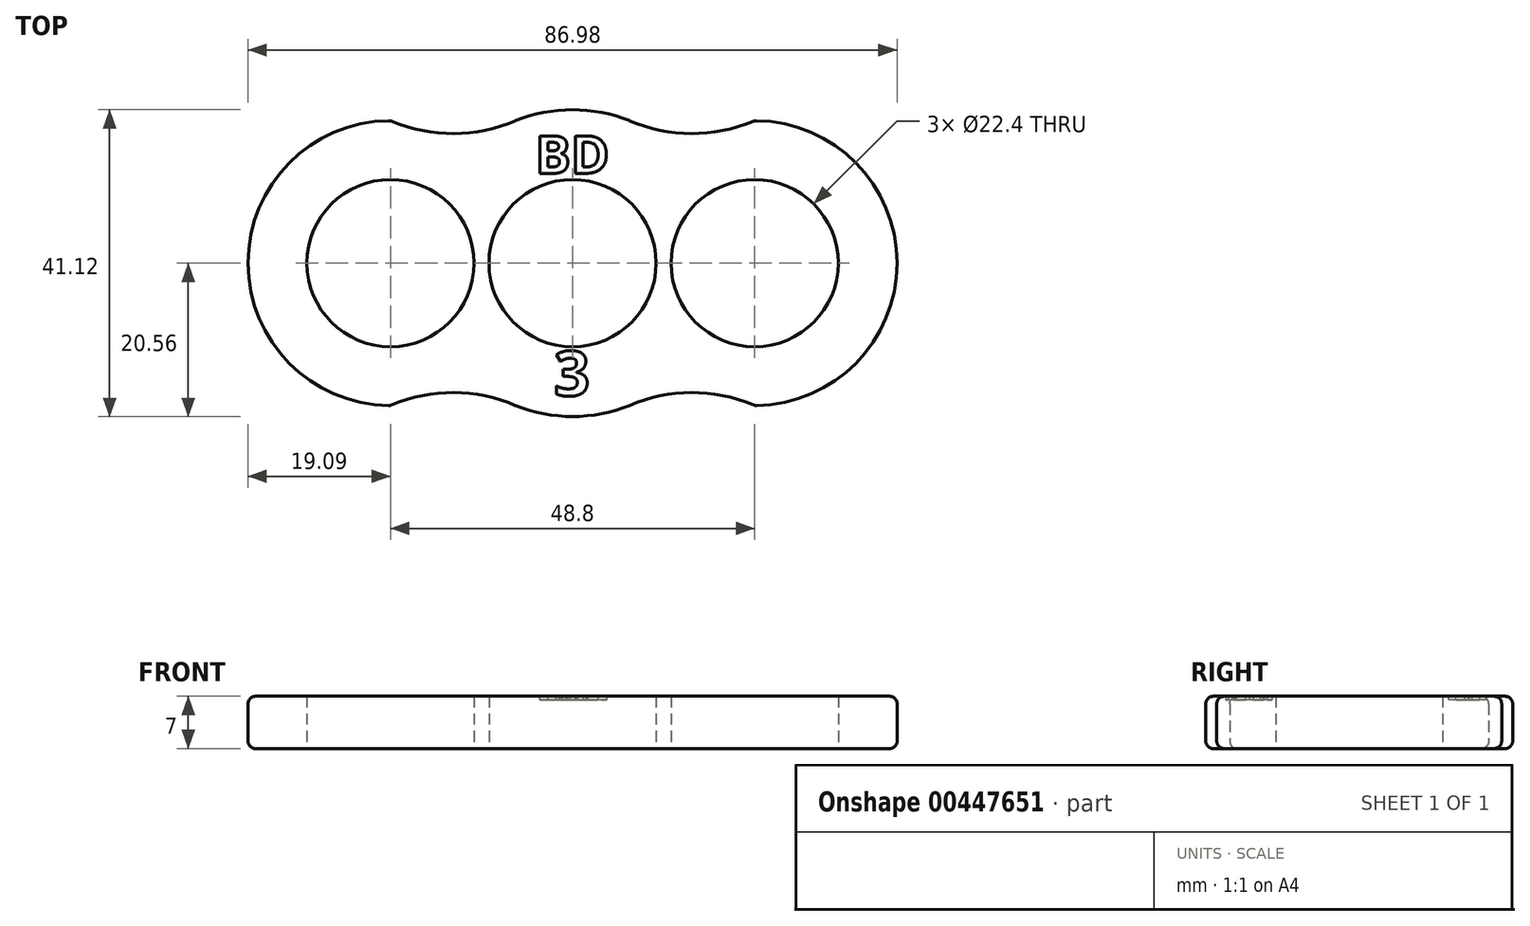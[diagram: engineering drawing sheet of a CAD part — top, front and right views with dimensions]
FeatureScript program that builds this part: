
annotation { "Feature Type Name" : "Feature", "Feature Type Description" : "" }
export const myFeature = defineFeature(function(context is Context, id is Id, definition is map)
    precondition{}
    {
        {
            var Q0;
            Q0=qCreatedBy(makeId("Top.planeOp"),FACE);
            var sketch = newSketch(context, id + "F0", { "sketchPlane" : qUnion([Q0])});
            skCircle(sketch, "E0", {"center": v(0, 0) * mm, "radius": 11.2 * mm});
            skCircle(sketch, "E1", {"center": v(-24.4, 0) * mm, "radius": 11.2 * mm});
            skCircle(sketch, "E2", {"center": v(24.4, 0) * mm, "radius": 11.2 * mm});
            skPoint(sketch, "E3", {"position": v(-13.2, 0) * mm});
            skPoint(sketch, "E4", {"position": v(-11.2, 0) * mm});
            skPoint(sketch, "E5", {"position": v(11.2, 0) * mm});
            skPoint(sketch, "E6", {"position": v(13.2, 0) * mm});
            skLineSegment(sketch, "E7", {"start": v(-13.2, 0) * mm, "end": v(-11.2, 0) * mm, "construction": true});
            skLineSegment(sketch, "E8", {"start": v(11.2, 0) * mm, "end": v(13.2, 0) * mm});
            skArc(sketch, "E9", {"start": v(-24.4, 19.09) * mm, "mid": v(-43.49, 0) * mm, "end": v(-24.4, -19.09) * mm});
            skArc(sketch, "E10", {"start": v(24.4, 19.09) * mm, "mid": v(43.49, 0) * mm, "end": v(24.4, -19.09) * mm});
            skArc(sketch, "E11", {"start": v(7.64, 19.09) * mm, "mid": v(0, 20.56) * mm, "end": v(-7.64, 19.09) * mm});
            skArc(sketch, "E12", {"start": v(7.64, -19.09) * mm, "mid": v(0, -20.56) * mm, "end": v(-7.64, -19.09) * mm});
            skArc(sketch, "E13", {"start": v(-24.4, 19.09) * mm, "mid": v(-16.02, 17.36) * mm, "end": v(-7.64, 19.09) * mm});
            skArc(sketch, "E14", {"start": v(7.64, 19.09) * mm, "mid": v(16.02, 17.36) * mm, "end": v(24.4, 19.09) * mm});
            skArc(sketch, "E15", {"start": v(-7.64, -19.09) * mm, "mid": v(-16.02, -17.36) * mm, "end": v(-24.4, -19.09) * mm});
            skArc(sketch, "E16", {"start": v(24.4, -19.09) * mm, "mid": v(16.02, -17.36) * mm, "end": v(7.64, -19.09) * mm});
            skLineSegment(sketch, "E17", {"start": v(-24.4, -19.09) * mm, "end": v(-7.64, -19.09) * mm, "construction": true});
            skLineSegment(sketch, "E18", {"start": v(7.64, -19.09) * mm, "end": v(24.4, -19.09) * mm, "construction": true});
            skLineSegment(sketch, "E19", {"start": v(7.64, 19.09) * mm, "end": v(24.4, 19.09) * mm, "construction": true});
            skLineSegment(sketch, "E20", {"start": v(-24.4, 19.09) * mm, "end": v(-7.64, 19.09) * mm, "construction": true});
            skLineSegment(sketch, "E21", {"start": v(24.4, 19.09) * mm, "end": v(16.02, 38.5) * mm, "construction": true});
            skLineSegment(sketch, "E22", {"start": v(-24.4, 19.09) * mm, "end": v(-16.02, 38.5) * mm, "construction": true});
            skLineSegment(sketch, "E23", {"start": v(-24.4, -19.09) * mm, "end": v(-16.02, -38.5) * mm, "construction": true});
            skLineSegment(sketch, "E24", {"start": v(24.4, -19.09) * mm, "end": v(16.02, -38.5) * mm, "construction": true});
            skSolve(sketch);
        }
        {
            var Q0;
            Q0=makeQuery(id+"F0.imprint","IMPRINT",FACE,{"disambiguationData":[TD([[makeQuery(id+"F0.imprint","IMPRINT",EDGE,{"derivedFrom":sQuery(id+"F0.wireOp",EDGE,"E0")}),-1.0]])]});
            extrude(context, id + "F1", {"entities" : qUnion([Q0]), "depth" : 7 * mm, "offsetDistance" : 25.4 * mm});
        }
        {
            var Q0;
            Q0=makeQuery(id+"F1.opExtrude","CAP_FACE",FACE,{"disambiguationData":[OSD([sQuery(id+"F0.wireOp",EDGE,"E0"),sQuery(id+"F0.wireOp",EDGE,"E1"),sQuery(id+"F0.wireOp",EDGE,"E2"),sQuery(id+"F0.wireOp",EDGE,"E9"),sQuery(id+"F0.wireOp",EDGE,"E10"),sQuery(id+"F0.wireOp",EDGE,"E11"),sQuery(id+"F0.wireOp",EDGE,"E12"),sQuery(id+"F0.wireOp",EDGE,"E13"),sQuery(id+"F0.wireOp",EDGE,"E14"),sQuery(id+"F0.wireOp",EDGE,"E15"),sQuery(id+"F0.wireOp",EDGE,"E16")])],"isStart":false});
            var sketch = newSketch(context, id + "F2", { "sketchPlane" : qUnion([Q0])});
            skText(sketch, "E25", { "text": "BD", "fontName": "NotoSans-Bold.ttf"});
            skLineSegment(sketch, "E26", {"start": v(-7.64, 19.09) * mm, "end": v(0, 17.1) * mm, "construction": true});
            skLineSegment(sketch, "E27", {"start": v(7.64, 19.09) * mm, "end": v(0, 17.1) * mm, "construction": true});
            skText(sketch, "E28", { "text": "3", "fontName": "NotoSans-Bold.ttf"});
            skLineSegment(sketch, "E29", {"start": v(2.5, -18.17) * mm, "end": v(7.64, -19.09) * mm, "construction": true});
            skLineSegment(sketch, "E30", {"start": v(-2.5, -18.17) * mm, "end": v(-7.64, -19.09) * mm, "construction": true});
            const initialGuessF2  = {"E25": [-0.005, 0.01203, 1, 0, 0.00507], "E28": [-0.0025, -0.01778, 1, 0, 0.00603]};
            skSetInitialGuess(sketch, initialGuessF2);
            skSolve(sketch);
        }
        {
            var Q0;
            Q0=makeQuery(id+"F2.imprint","IMPRINT",FACE,{"disambiguationData":[TD([[makeQuery(id+"F2.imprint","IMPRINT",EDGE,{"derivedFrom":sQuery(id+"F2.wireOp",EDGE,"E25.sketch_text.stroke-0")}),-1.0]])]});
            var Q1;
            Q1 = qSketchRegion(id + "F2", true);
            extrude(context, id + "F3", {"entities" : qUnion([Q0, Q1]), "operationType" : NewBodyOperationType.REMOVE, "oppositeDirection" : true, "depth" : .5 * mm, "offsetDistance" : 25.4 * mm, "hasDraft" : true, "draftAngle" : 3 * degree});
        }
        {
            var Q0;
            Q0=makeQuery(id+"F1.opExtrude","SWEPT_FACE",FACE,{"disambiguationData":[OSD([sQuery(id+"F0.wireOp",EDGE,"E9")])]});
            var Q1;
            Q1=makeQuery(id+"F1.opExtrude","SWEPT_FACE",FACE,{"disambiguationData":[OSD([sQuery(id+"F0.wireOp",EDGE,"E15")])]});
            var Q2;
            Q2=makeQuery(id+"F1.opExtrude","SWEPT_FACE",FACE,{"disambiguationData":[OSD([sQuery(id+"F0.wireOp",EDGE,"E12")])]});
            var Q3;
            Q3=makeQuery(id+"F1.opExtrude","SWEPT_FACE",FACE,{"disambiguationData":[OSD([sQuery(id+"F0.wireOp",EDGE,"E16")])]});
            var Q4;
            Q4=makeQuery(id+"F1.opExtrude","SWEPT_FACE",FACE,{"disambiguationData":[OSD([sQuery(id+"F0.wireOp",EDGE,"E10")])]});
            var Q5;
            Q5=makeQuery(id+"F1.opExtrude","SWEPT_FACE",FACE,{"disambiguationData":[OSD([sQuery(id+"F0.wireOp",EDGE,"E14")])]});
            var Q6;
            Q6=makeQuery(id+"F1.opExtrude","SWEPT_FACE",FACE,{"disambiguationData":[OSD([sQuery(id+"F0.wireOp",EDGE,"E11")])]});
            var Q7;
            Q7=makeQuery(id+"F1.opExtrude","SWEPT_FACE",FACE,{"disambiguationData":[OSD([sQuery(id+"F0.wireOp",EDGE,"E13")])]});
            fillet(context, id + "F4", {"entities" : qUnion([Q0, Q1, Q2, Q3, Q4, Q5, Q6, Q7]), "radius" : 1 * mm, "tangentPropagation" : true, "allowEdgeOverflow" : false});
        }
    });
